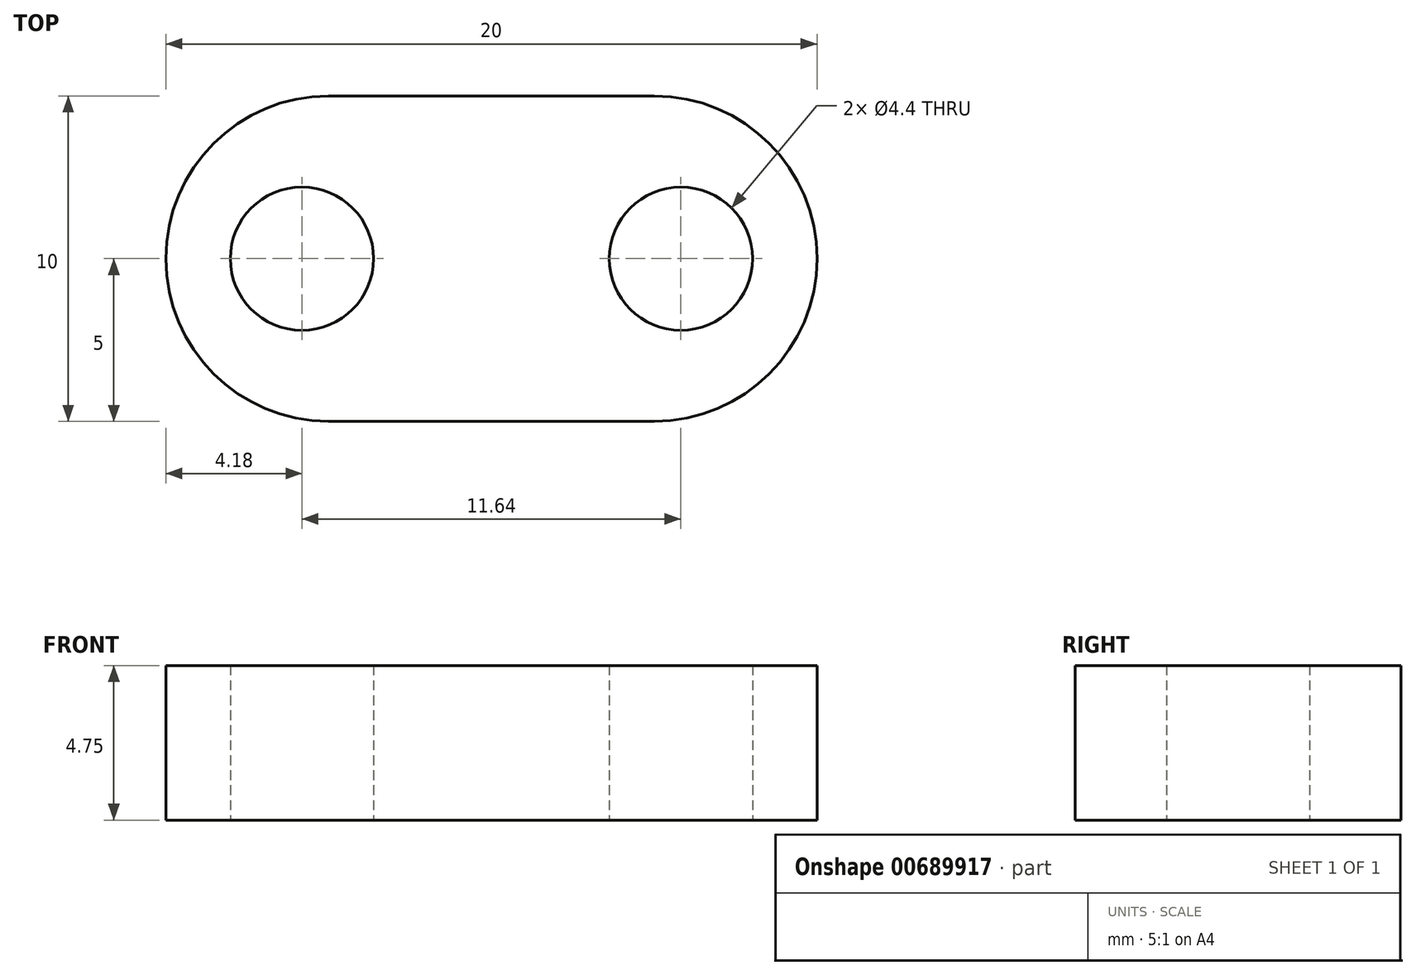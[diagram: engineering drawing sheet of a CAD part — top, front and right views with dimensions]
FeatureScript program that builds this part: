
annotation { "Feature Type Name" : "Feature", "Feature Type Description" : "" }
export const myFeature = defineFeature(function(context is Context, id is Id, definition is map)
    precondition{}
    {
        {
            var Q0;
            Q0=qCreatedBy(makeId("Top.planeOp"),FACE);
            var sketch = newSketch(context, id + "F0", { "sketchPlane" : qUnion([Q0])});
            skLineSegment(sketch, "E0.bottom", {"start": v(-10, 5) * mm, "end": v(10, 5) * mm});
            skLineSegment(sketch, "E0.top", {"start": v(-10, -5) * mm, "end": v(10, -5) * mm});
            skLineSegment(sketch, "E0.left", {"start": v(-10, 5) * mm, "end": v(-10, -5) * mm});
            skLineSegment(sketch, "E0.right", {"start": v(10, 5) * mm, "end": v(10, -5) * mm});
            skPoint(sketch, "E0.middle", {"position": v(0, 0) * mm});
            skPoint(sketch, "E1", {"position": v(-5.82, 0) * mm});
            skPoint(sketch, "E1.positionSnap0", {"position": v(-10, 0) * mm});
            skPoint(sketch, "E2", {"position": v(5.82, 0) * mm});
            skSolve(sketch);
        }
        {
            var Q0;
            Q0=makeQuery(id+"F0.imprint","IMPRINT",FACE,{"disambiguationData":[TD([[makeQuery(id+"F0.imprint","IMPRINT",EDGE,{"derivedFrom":sQuery(id+"F0.wireOp",EDGE,"E0.bottom")}),-1.0]])]});
            extrude(context, id + "F1", {"entities" : qUnion([Q0]), "depth" : 4.75 * mm, "offsetDistance" : 25 * mm});
        }
        {
            var Q0;
            Q0=sQuery(id+"F0.wireOp",VERTEX,"E1");
            var Q1;
            Q1=sQuery(id+"F0.wireOp",VERTEX,"E2");
            var Q2;
            Q2=makeQuery(id+"F1.opExtrude","SWEPT_BODY",BODY,{"disambiguationData":[OSD([sQuery(id+"F0.wireOp",EDGE,"E0.bottom"),sQuery(id+"F0.wireOp",EDGE,"E0.top"),sQuery(id+"F0.wireOp",EDGE,"E0.left"),sQuery(id+"F0.wireOp",EDGE,"E0.right")])]});
            hole(context, id + "F2", {"style" : HoleStyle.SIMPLE, "endStyle" : HoleEndStyle.BLIND, "oppositeDirection" : true, "standardTappedOrClearance" : lookupTablePath({ "standard" : "ISO", "fit" : "Normal", "size" : "M4", "type" : "Clearance" }), "standardBlindInLast" : lookupTablePath({ "fit" : "Standard", "standard" : "ISO", "size" : "M4", "type" : "Clearance" }), "holeDiameter" : 4.4 * mm, "majorDiameter" : 5 * mm, "holeDepth" : 25 * mm, "isTappedThrough" : true, "tappedDepth" : 12 * mm, "tapClearance" : 3, "locations" : qUnion([Q0, Q1]), "scope" : qUnion([Q2])});
        }
        {
            var Q0;
            Q0=makeQuery(id+"F1.opExtrude","SWEPT_EDGE",EDGE,{"disambiguationData":[OSD([sQuery(id+"F0.wireOp",EDGE,"E0.bottom"),sQuery(id+"F0.wireOp",EDGE,"E0.right")])]});
            var Q1;
            Q1=makeQuery(id+"F1.opExtrude","SWEPT_EDGE",EDGE,{"disambiguationData":[OSD([sQuery(id+"F0.wireOp",EDGE,"E0.top"),sQuery(id+"F0.wireOp",EDGE,"E0.right")])]});
            var Q2;
            Q2=makeQuery(id+"F1.opExtrude","SWEPT_EDGE",EDGE,{"disambiguationData":[OSD([sQuery(id+"F0.wireOp",EDGE,"E0.bottom"),sQuery(id+"F0.wireOp",EDGE,"E0.left")])]});
            var Q3;
            Q3=makeQuery(id+"F1.opExtrude","SWEPT_EDGE",EDGE,{"disambiguationData":[OSD([sQuery(id+"F0.wireOp",EDGE,"E0.top"),sQuery(id+"F0.wireOp",EDGE,"E0.left")])]});
            fillet(context, id + "F3", {"entities" : qUnion([Q0, Q1, Q2, Q3]), "radius" : 5 * mm, "tangentPropagation" : true, "allowEdgeOverflow" : false});
        }
    });
